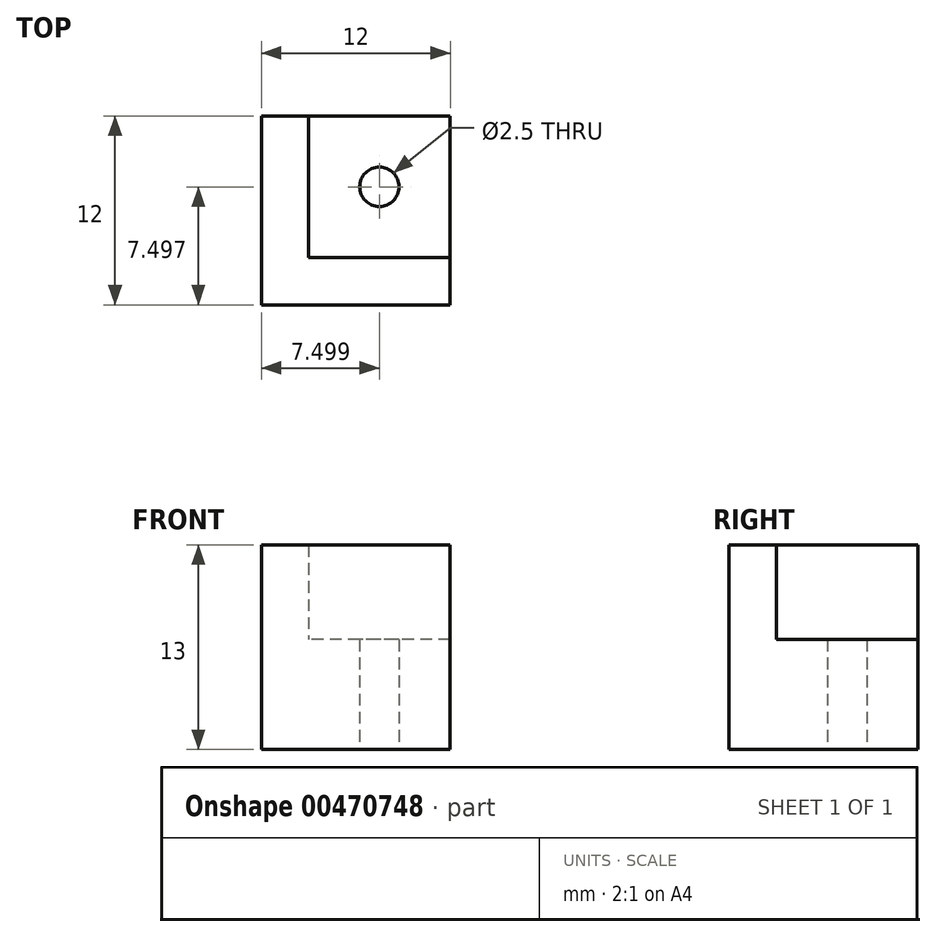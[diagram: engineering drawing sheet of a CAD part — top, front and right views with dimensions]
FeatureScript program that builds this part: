
annotation { "Feature Type Name" : "Feature", "Feature Type Description" : "" }
export const myFeature = defineFeature(function(context is Context, id is Id, definition is map)
    precondition{}
    {
        {
            var Q0;
            Q0=qCreatedBy(makeId("Top.planeOp"),FACE);
            var sketch = newSketch(context, id + "F0", { "sketchPlane" : qUnion([Q0])});
            skLineSegment(sketch, "E0.bottom", {"start": v(-37.57, 16.84) * mm, "end": v(-49.57, 16.84) * mm});
            skLineSegment(sketch, "E0.top", {"start": v(-37.57, 28.84) * mm, "end": v(-49.57, 28.84) * mm});
            skLineSegment(sketch, "E0.left", {"start": v(-37.57, 16.84) * mm, "end": v(-37.57, 28.84) * mm});
            skLineSegment(sketch, "E0.right", {"start": v(-49.57, 16.84) * mm, "end": v(-49.57, 28.84) * mm});
            skPoint(sketch, "E0.middle", {"position": v(-43.57, 22.84) * mm});
            skLineSegment(sketch, "E1", {"start": v(-46.57, 28.84) * mm, "end": v(-46.57, 19.84) * mm});
            skLineSegment(sketch, "E2", {"start": v(-46.57, 19.84) * mm, "end": v(-37.57, 19.84) * mm});
            skCircle(sketch, "E3", {"center": v(-42.07, 24.34) * mm, "radius": 1.25 * mm});
            skPoint(sketch, "E3.centerSnap0", {"position": v(-42.07, 19.84) * mm});
            skPoint(sketch, "E3.centerSnap1", {"position": v(-46.57, 24.34) * mm});
            skSolve(sketch);
        }
        {
            var Q0;
            {var subQ4=sQuery(id+"F0.wireOp",EDGE,"E1");Q0=makeQuery(id+"F0.imprint","IMPRINT",FACE,{"disambiguationData":[TD([[makeQuery(id+"F0.imprint","IMPRINT",EDGE,{"derivedFrom":subQ4}),1.0]])]});}
            var Q1;
            {var subQ1=sQuery(id+"F0.wireOp",EDGE,"E0.bottom");Q1=makeQuery(id+"F0.imprint","IMPRINT",FACE,{"disambiguationData":[TD([[makeQuery(id+"F0.imprint","IMPRINT",EDGE,{"derivedFrom":subQ1}),-1.0]])]});}
            extrude(context, id + "F1", {"entities" : qUnion([Q0, Q1]), "depth" : 7 * mm, "offsetDistance" : 25 * mm});
        }
        {
            var Q0;
            {var subQ1=sQuery(id+"F0.wireOp",EDGE,"E0.bottom");Q0=makeQuery(id+"F0.imprint","IMPRINT",FACE,{"disambiguationData":[TD([[makeQuery(id+"F0.imprint","IMPRINT",EDGE,{"derivedFrom":subQ1}),-1.0]])]});}
            extrude(context, id + "F2", {"entities" : qUnion([Q0]), "operationType" : NewBodyOperationType.ADD, "depth" : 13 * mm, "offsetDistance" : 25 * mm});
        }
    });
